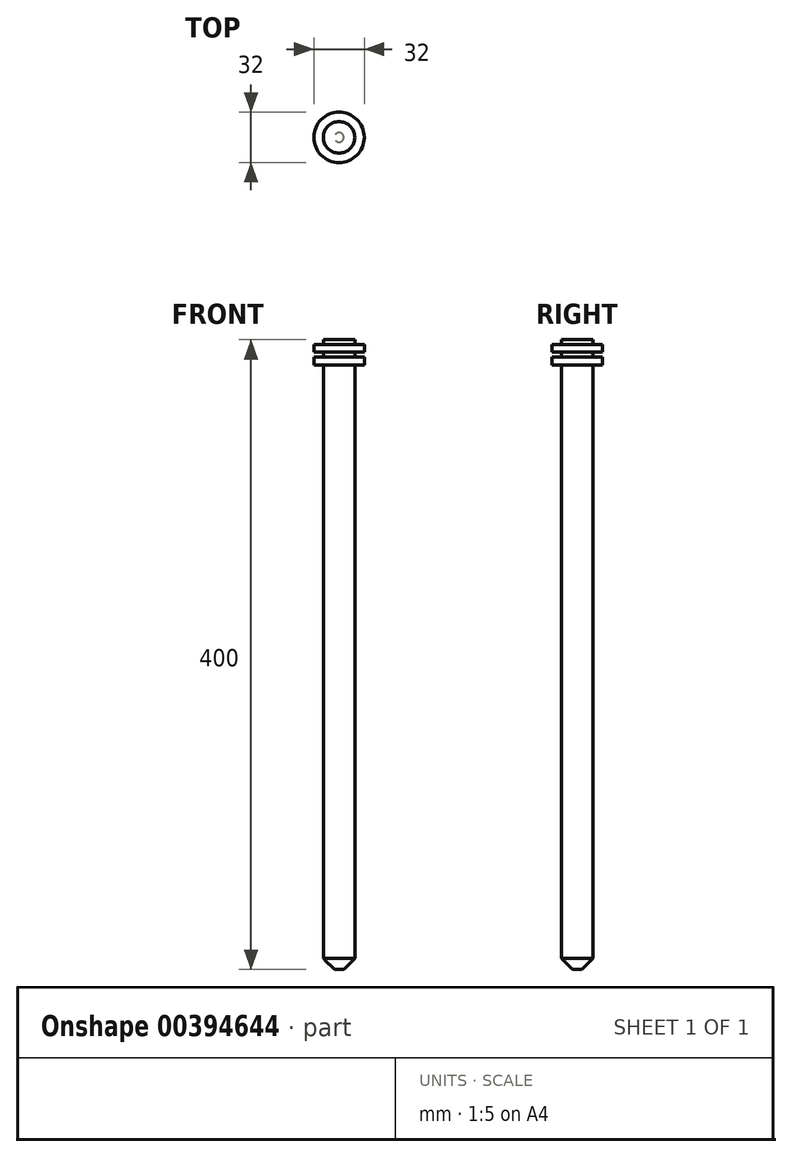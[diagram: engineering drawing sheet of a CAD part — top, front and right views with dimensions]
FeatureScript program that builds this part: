
annotation { "Feature Type Name" : "Feature", "Feature Type Description" : "" }
export const myFeature = defineFeature(function(context is Context, id is Id, definition is map)
    precondition{}
    {
        {
            var Q0;
            Q0=qCreatedBy(makeId("Right.planeOp"),FACE);
            var sketch = newSketch(context, id + "F0", { "sketchPlane" : qUnion([Q0])});
            skLineSegment(sketch, "E0.bottom", {"start": v(0, -256.56) * mm, "end": v(-10, -256.56) * mm});
            skLineSegment(sketch, "E0.top", {"start": v(0, 143.44) * mm, "end": v(-10, 143.44) * mm});
            skLineSegment(sketch, "E0.left", {"start": v(0, -256.56) * mm, "end": v(0, 143.44) * mm});
            skLineSegment(sketch, "E0.right", {"start": v(-10, -256.56) * mm, "end": v(-10, 127.44) * mm});
            skPoint(sketch, "E0.middle", {"position": v(0, 0) * mm});
            skLineSegment(sketch, "E1.bottom", {"start": v(-10, 140.44) * mm, "end": v(-16, 140.44) * mm});
            skLineSegment(sketch, "E1.top", {"start": v(-10, 135.44) * mm, "end": v(-16, 135.44) * mm});
            skLineSegment(sketch, "E1.right", {"start": v(-16, 140.44) * mm, "end": v(-16, 135.44) * mm});
            skLineSegment(sketch, "E2.bottom", {"start": v(-10, 132.44) * mm, "end": v(-16, 132.44) * mm});
            skLineSegment(sketch, "E2.top", {"start": v(-10, 127.44) * mm, "end": v(-16, 127.44) * mm});
            skLineSegment(sketch, "E2.right", {"start": v(-16, 132.44) * mm, "end": v(-16, 127.44) * mm});
            skLineSegment(sketch, "E3.trimOffspring", {"start": v(-10, 140.44) * mm, "end": v(-10, 143.44) * mm});
            skLineSegment(sketch, "E4.trimOffspring", {"start": v(-10, 132.44) * mm, "end": v(-10, 135.44) * mm});
            skSolve(sketch);
        }
        {
            var Q0;
            Q0=makeQuery(id+"F0.imprint","IMPRINT",FACE,{"disambiguationData":[TD([[makeQuery(id+"F0.imprint","IMPRINT",EDGE,{"derivedFrom":sQuery(id+"F0.wireOp",EDGE,"E0.bottom")}),-1.0]])]});
            var Q1;
            Q1=sQuery(id+"F0.wireOp",EDGE,"E0.left");
            revolve(context, id + "F1", {"surfaceOperationType" : NewSurfaceOperationType.NEW, "entities" : qUnion([Q0]), "axis" : qUnion([Q1]), "revolveType" : RevolveType.FULL});
        }
        {
            var Q0;
            Q0=makeQuery(id+"F1.opRevolve","SWEPT_EDGE",EDGE,{"disambiguationData":[OSD([sQuery(id+"F0.wireOp",EDGE,"E0.bottom"),sQuery(id+"F0.wireOp",EDGE,"E0.right")])]});
            chamfer(context, id + "F2", {"entities" : qUnion([Q0]), "width" : 7 * mm, "tangentPropagation" : true});
        }
    });
